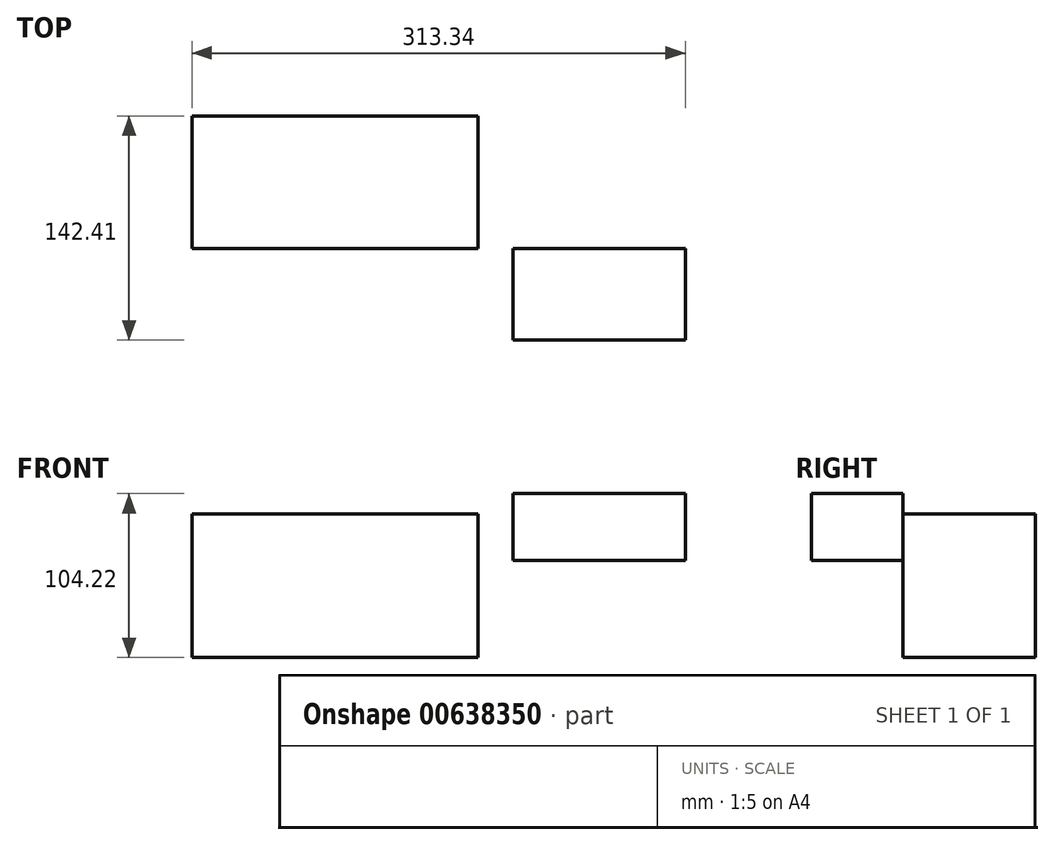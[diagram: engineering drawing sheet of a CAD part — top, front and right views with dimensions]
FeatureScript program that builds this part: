
annotation { "Feature Type Name" : "Feature", "Feature Type Description" : "" }
export const myFeature = defineFeature(function(context is Context, id is Id, definition is map)
    precondition{}
    {
        {
            var Q0;
            Q0=qCreatedBy(makeId("Top.planeOp"),FACE);
            var sketch = newSketch(context, id + "F0", { "sketchPlane" : qUnion([Q0])});
            skLineSegment(sketch, "E0.bottom", {"start": v(-126.07, -10.28) * mm, "end": v(55.77, -10.28) * mm});
            skLineSegment(sketch, "E0.top", {"start": v(-126.07, -94.52) * mm, "end": v(55.77, -94.52) * mm});
            skLineSegment(sketch, "E0.left", {"start": v(-126.07, -10.28) * mm, "end": v(-126.07, -94.52) * mm});
            skLineSegment(sketch, "E0.right", {"start": v(55.77, -10.28) * mm, "end": v(55.77, -94.52) * mm});
            skSolve(sketch);
        }
        {
            var Q0;
            Q0 = qSketchRegion(id + "F0", true);
            extrude(context, id + "F1", {"entities" : qUnion([Q0]), "depth" : 91.19 * mm, "offsetDistance" : 25.4 * mm});
        }
        {
            var Q0;
            Q0=makeQuery(id+"F1.opExtrude","SWEPT_FACE",FACE,{"disambiguationData":[OSD([sQuery(id+"F0.wireOp",EDGE,"E0.top")])]});
            var sketch = newSketch(context, id + "F2", { "sketchPlane" : qUnion([Q0])});
            skLineSegment(sketch, "E1.bottom", {"start": v(77.97, 61.74) * mm, "end": v(187.27, 61.74) * mm});
            skLineSegment(sketch, "E1.top", {"start": v(77.97, 104.22) * mm, "end": v(187.27, 104.22) * mm});
            skLineSegment(sketch, "E1.left", {"start": v(77.97, 61.74) * mm, "end": v(77.97, 104.22) * mm});
            skLineSegment(sketch, "E1.right", {"start": v(187.27, 61.74) * mm, "end": v(187.27, 104.22) * mm});
            skSolve(sketch);
        }
        {
            var Q0;
            Q0 = qSketchRegion(id + "F2", true);
            extrude(context, id + "F3", {"entities" : qUnion([Q0]), "depth" : 58.17 * mm, "offsetDistance" : 25.4 * mm});
        }
    });
